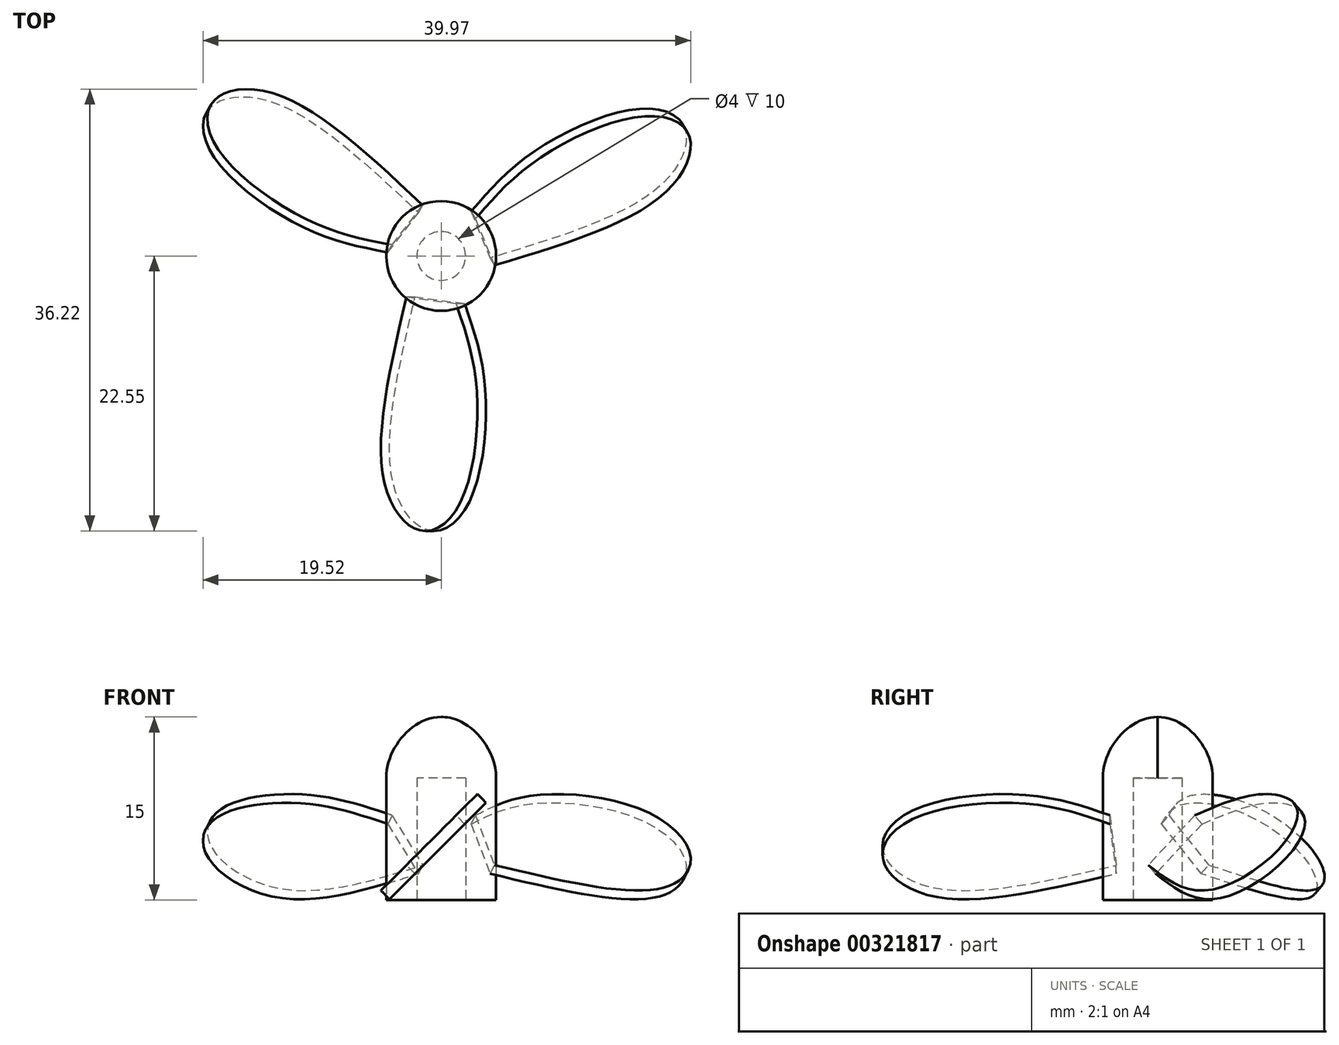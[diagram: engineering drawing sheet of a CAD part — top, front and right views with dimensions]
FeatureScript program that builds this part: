
annotation { "Feature Type Name" : "Feature", "Feature Type Description" : "" }
export const myFeature = defineFeature(function(context is Context, id is Id, definition is map)
    precondition{}
    {
        {
            var Q0;
            Q0=qCreatedBy(makeId("Top.planeOp"),FACE);
            var sketch = newSketch(context, id + "F0", { "sketchPlane" : qUnion([Q0])});
            skCircle(sketch, "E0", {"center": v(0, 0) * mm, "radius": 20 * mm, "construction": true});
            skCircle(sketch, "E1", {"center": v(0, 0) * mm, "radius": 4.5 * mm});
            skCircle(sketch, "E2", {"center": v(0, 0) * mm, "radius": 2 * mm});
            skSolve(sketch);
        }
        {
            var Q0;
            Q0 = qSketchRegion(id + "F0", true);
            extrude(context, id + "F1", {"entities" : qUnion([Q0]), "depth" : 10 * mm});
        }
        {
            var Q0;
            Q0=qCreatedBy(makeId("Front.planeOp"),FACE);
            var sketch = newSketch(context, id + "F2", { "sketchPlane" : qUnion([Q0])});
            skLineSegment(sketch, "E3", {"start": v(0, 15) * mm, "end": v(0, 10) * mm});
            skLineSegment(sketch, "E4", {"start": v(0, 10) * mm, "end": v(4.5, 10) * mm});
            skFitSpline(sketch, "E5", {"points": [v(0, 15) * mm, v(1.82, 14.5) * mm, v(4.5, 10) * mm], "startDerivative": vector(3.13, 0) * mm, "endDerivative": vector(0, -10.08) * mm});
            skSolve(sketch);
        }
        {
            var Q0;
            Q0=makeQuery(id+"F2.imprint","IMPRINT",FACE,{"disambiguationData":[TD([[makeQuery(id+"F2.imprint","IMPRINT",EDGE,{"derivedFrom":sQuery(id+"F2.wireOp",EDGE,"E3")}),1.0]])]});
            var Q1;
            Q1=sQuery(id+"F2.wireOp",EDGE,"E3");
            revolve(context, id + "F3", {"operationType" : NewBodyOperationType.ADD, "entities" : qUnion([Q0]), "axis" : qUnion([Q1]), "revolveType" : RevolveType.FULL});
        }
        {
            var Q0;
            Q0=qCreatedBy(makeId("Front.planeOp"),FACE);
            var sketch = newSketch(context, id + "F4", { "sketchPlane" : qUnion([Q0])});
            skLineSegment(sketch, "E6", {"start": v(-4.2, 9.2) * mm, "end": v(4.2, 0.8) * mm, "construction": true});
            skLineSegment(sketch, "E7", {"start": v(0, 5) * mm, "end": v(0, 0) * mm, "construction": true});
            skSolve(sketch);
        }
        {
            var Q0;
            Q0=sQuery(id+"F4.wireOp",EDGE,"E6");
            cPoint(context, id + "F5", {"entities" : qUnion([Q0]), "parameter" : 0.5});
        }
        {
            var Q0;
            Q0=sQuery(id+"F4.wireOp",EDGE,"E6");
            var Q1;
            Q1 = qCreatedBy(id + "F5" ,VERTEX);
            cPlane(context, id + "F6", {"entities" : qUnion([Q0, Q1]), "cplaneType" : CPlaneType.LINE_POINT, "offset" : 25 * mm, "width" : 150 * mm, "height" : 150 * mm});
        }
        {
            var Q0;
            Q0=qCreatedBy(id+"F6.planeOp",FACE);
            var sketch = newSketch(context, id + "F7", { "sketchPlane" : qUnion([Q0])});
            skFitSpline(sketch, "E8", {"points": [v(-3.93, 5.76) * mm, v(-10.75, 8.12) * mm, v(-20.14, 6.3) * mm, v(-22.5, 1.58) * mm, v(-18.18, -2.68) * mm, v(-3.4, 0) * mm], "startDerivative": vector(-33.23, 16.46) * mm, "endDerivative": vector(61.66, 20.48) * mm});
            skLineSegment(sketch, "E9", {"start": v(-3.93, 5.76) * mm, "end": v(-3.4, 0) * mm});
            skSolve(sketch);
        }
        {
            var Q0;
            Q0=makeQuery(id+"F7.imprint","IMPRINT",FACE,{"disambiguationData":[TD([[makeQuery(id+"F7.imprint","IMPRINT",EDGE,{"derivedFrom":sQuery(id+"F7.wireOp",EDGE,"E8")}),1.0]])]});
            extrude(context, id + "F8", {"entities" : qUnion([Q0]), "depth" : 0.5 * mm, "hasSecondDirection" : true, "secondDirectionOppositeDirection" : true, "secondDirectionDepth" : 0.5 * mm});
        }
        {
            var Q0;
            Q0=qCreatedBy(makeId("Front.planeOp"),FACE);
            var sketch = newSketch(context, id + "F9", { "sketchPlane" : qUnion([Q0])});
            skLineSegment(sketch, "E10", {"start": v(0, 0) * mm, "end": v(0, 8.52) * mm, "construction": true});
            skSolve(sketch);
        }
        {
            var Q0;
            Q0=makeQuery(id+"F8.opExtrude","SWEPT_BODY",BODY,{"disambiguationData":[OSD([sQuery(id+"F7.wireOp",EDGE,"E8"),sQuery(id+"F7.wireOp",EDGE,"E9")])]});
            var Q1;
            Q1=sQuery(id+"F9.wireOp",EDGE,"E10");
            circularPattern(context, id + "F10", {"entities" : qUnion([Q0]), "axis" : qUnion([Q1]), "angle" : 360 * degree, "instanceCount" : 3, "equalSpace" : true});
        }
    });
